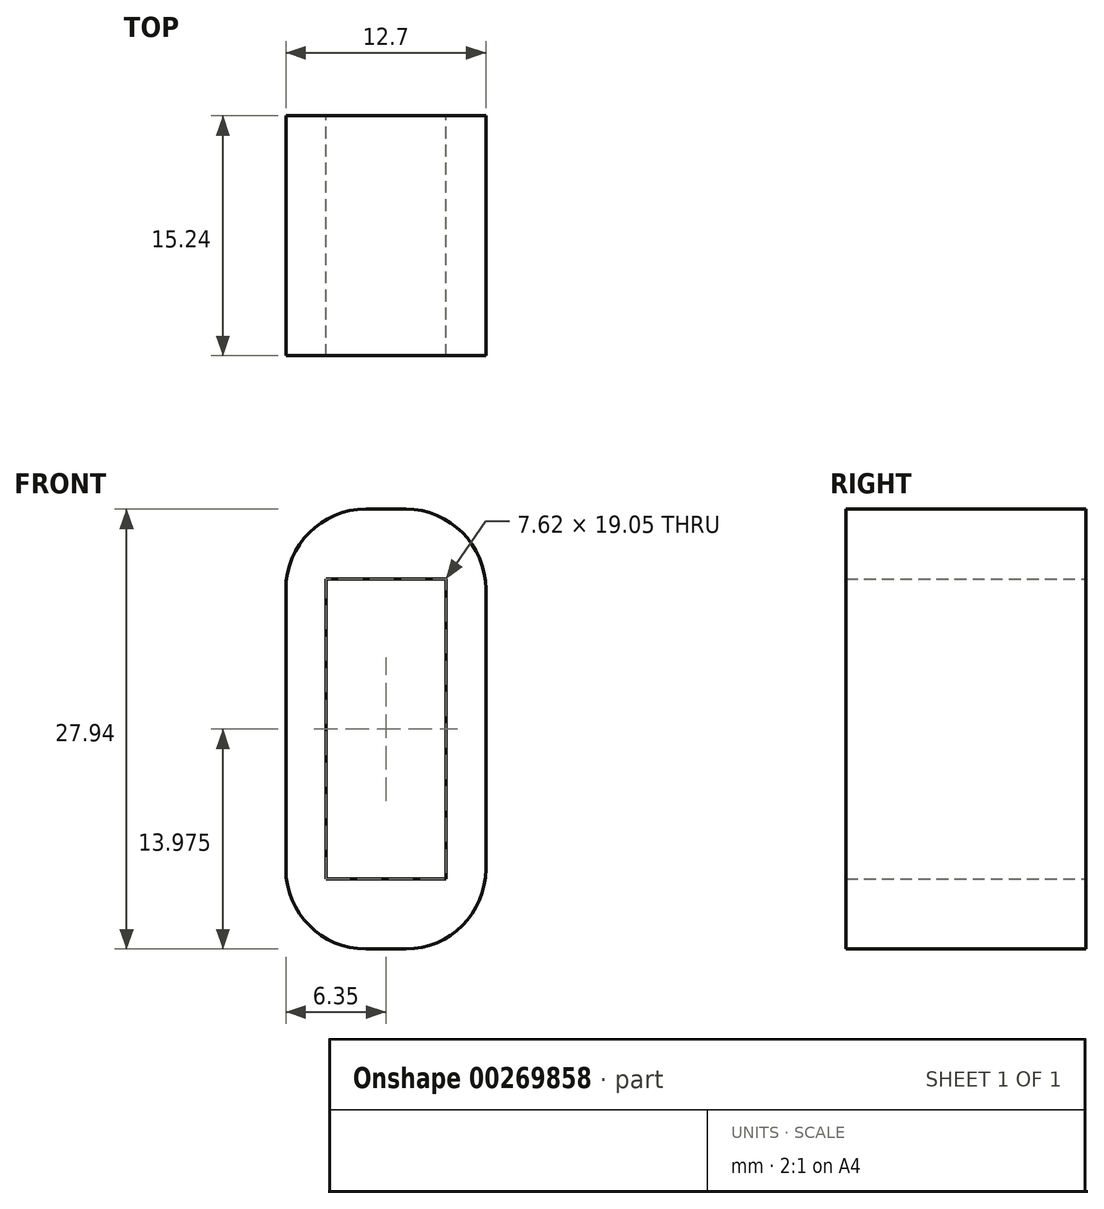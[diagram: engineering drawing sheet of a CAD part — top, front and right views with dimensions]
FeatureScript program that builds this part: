
annotation { "Feature Type Name" : "Feature", "Feature Type Description" : "" }
export const myFeature = defineFeature(function(context is Context, id is Id, definition is map)
    precondition{}
    {
        {
            var Q0;
            Q0=qCreatedBy(makeId("Front.planeOp"),FACE);
            var sketch = newSketch(context, id + "F0", { "sketchPlane" : qUnion([Q0])});
            skLineSegment(sketch, "E0.bottom", {"start": v(0, 0) * mm, "end": v(7.62, 0) * mm});
            skLineSegment(sketch, "E0.top", {"start": v(0, 19.05) * mm, "end": v(7.62, 19.05) * mm});
            skLineSegment(sketch, "E0.left", {"start": v(0, 0) * mm, "end": v(0, 19.05) * mm});
            skLineSegment(sketch, "E0.right", {"start": v(7.62, 0) * mm, "end": v(7.62, 19.05) * mm});
            skLineSegment(sketch, "E1.bottom", {"start": v(5.08, 23.5) * mm, "end": v(2.54, 23.5) * mm});
            skLineSegment(sketch, "E1.top", {"start": v(5.08, -4.45) * mm, "end": v(2.54, -4.45) * mm});
            skLineSegment(sketch, "E1.left", {"start": v(10.16, 18.41) * mm, "end": v(10.16, 0.63) * mm});
            skLineSegment(sketch, "E1.right", {"start": v(-2.54, 18.41) * mm, "end": v(-2.54, 0.63) * mm});
            skPoint(sketch, "E1.middle", {"position": v(3.8, 9.52) * mm});
            skPoint(sketch, "E2.visualSharp", {"position": v(-2.54, 23.5) * mm});
            skArc(sketch, "E2.filletArc", {"start": v(2.54, 23.5) * mm, "mid": v(-1.05, 22) * mm, "end": v(-2.54, 18.41) * mm});
            skPoint(sketch, "E3.visualSharp", {"position": v(10.16, 23.5) * mm});
            skArc(sketch, "E3.filletArc", {"start": v(10.16, 18.41) * mm, "mid": v(8.67, 22) * mm, "end": v(5.08, 23.5) * mm});
            skPoint(sketch, "E4.visualSharp", {"position": v(10.16, -4.45) * mm});
            skArc(sketch, "E4.filletArc", {"start": v(5.08, -4.45) * mm, "mid": v(8.67, -2.96) * mm, "end": v(10.16, 0.63) * mm});
            skPoint(sketch, "E5.visualSharp", {"position": v(-2.54, -4.45) * mm});
            skArc(sketch, "E5.filletArc", {"start": v(-2.54, 0.63) * mm, "mid": v(-1.05, -2.96) * mm, "end": v(2.54, -4.45) * mm});
            skSolve(sketch);
        }
        {
            var Q0;
            Q0=makeQuery(id+"F0.imprint","IMPRINT",FACE,{"disambiguationData":[TD([[makeQuery(id+"F0.imprint","IMPRINT",EDGE,{"derivedFrom":sQuery(id+"F0.wireOp",EDGE,"E0.bottom")}),-1.0]])]});
            extrude(context, id + "F1", {"entities" : qUnion([Q0]), "depth" : 15.24 * mm});
        }
    });
